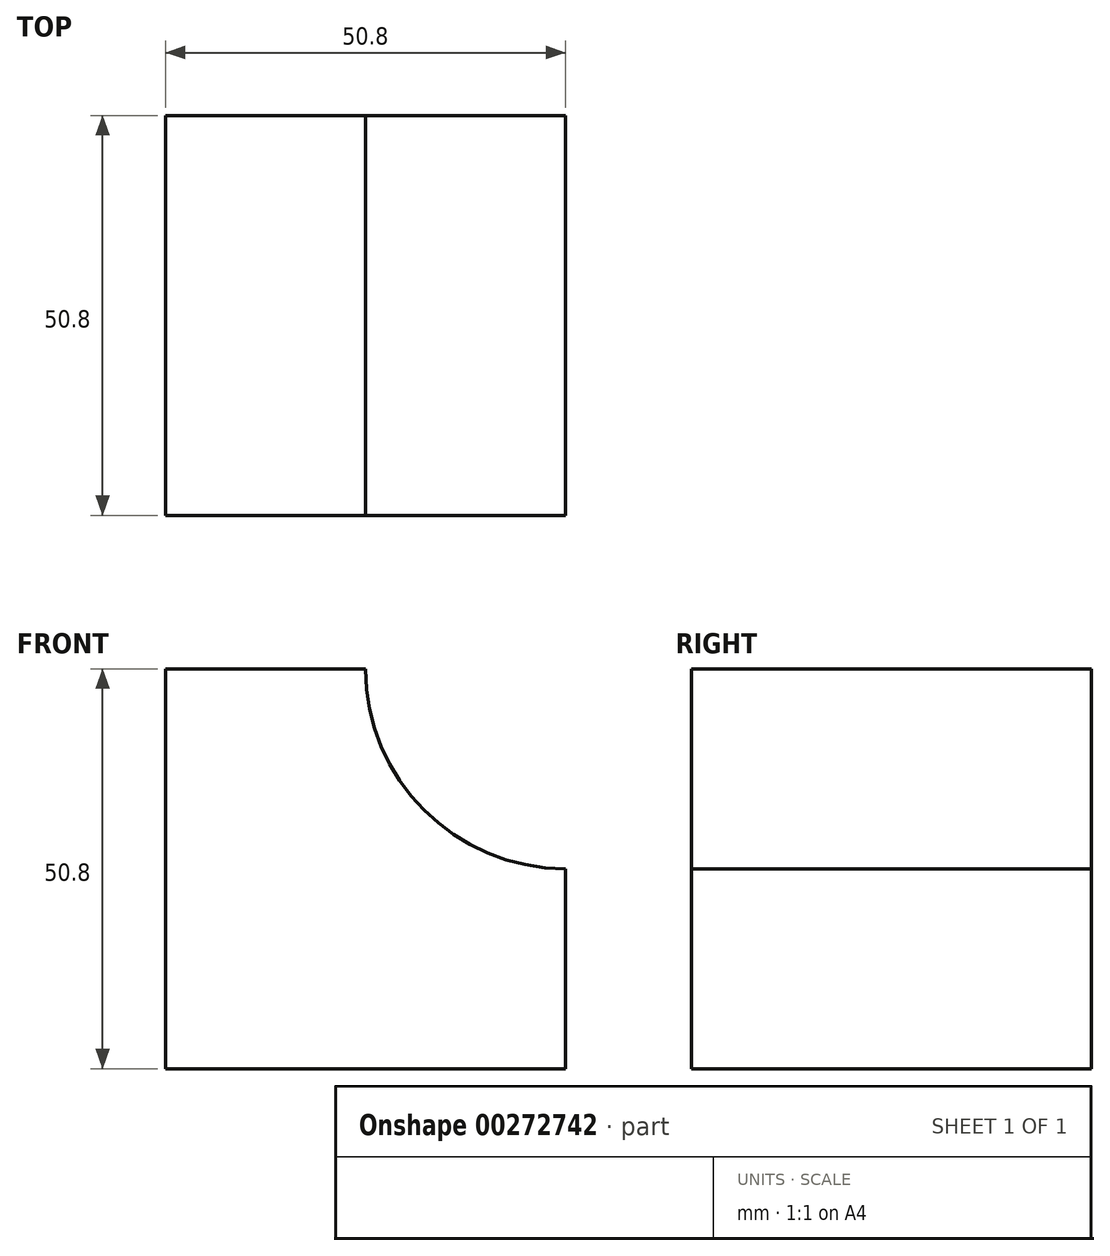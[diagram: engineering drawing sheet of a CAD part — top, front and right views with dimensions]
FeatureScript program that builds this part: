
annotation { "Feature Type Name" : "Feature", "Feature Type Description" : "" }
export const myFeature = defineFeature(function(context is Context, id is Id, definition is map)
    precondition{}
    {
        {
            var Q0;
            Q0=qCreatedBy(makeId("Front.planeOp"),FACE);
            var sketch = newSketch(context, id + "F0", { "sketchPlane" : qUnion([Q0])});
            skLineSegment(sketch, "E0", {"start": v(0, 0) * mm, "end": v(-50.8, 0) * mm});
            skLineSegment(sketch, "E1", {"start": v(-50.8, 0) * mm, "end": v(-50.8, 50.8) * mm});
            skLineSegment(sketch, "E2", {"start": v(-50.8, 50.8) * mm, "end": v(-25.4, 50.8) * mm});
            skLineSegment(sketch, "E3", {"start": v(-25.4, 50.8) * mm, "end": v(-25.4, 25.4) * mm});
            skLineSegment(sketch, "E4", {"start": v(-25.4, 25.4) * mm, "end": v(0, 25.4) * mm});
            skLineSegment(sketch, "E5", {"start": v(0, 0) * mm, "end": v(0, 25.4) * mm});
            skArc(sketch, "E6", {"start": v(-25.4, 50.8) * mm, "mid": v(-17.96, 32.84) * mm, "end": v(0, 25.4) * mm});
            skSolve(sketch);
        }
        {
            var Q0;
            Q0=makeQuery(id+"F0.imprint","IMPRINT",FACE,{"disambiguationData":[TD([[makeQuery(id+"F0.imprint","IMPRINT",EDGE,{"derivedFrom":sQuery(id+"F0.wireOp",EDGE,"E0")}),-1.0]])]});
            var Q1;
            Q1=makeQuery(id+"F0.imprint","IMPRINT",FACE,{"disambiguationData":[TD([[makeQuery(id+"F0.imprint","IMPRINT",EDGE,{"derivedFrom":sQuery(id+"F0.wireOp",EDGE,"E3")}),1.0]])]});
            extrude(context, id + "F1", {"entities" : qUnion([Q0, Q1]), "depth" : 50.8 * mm});
        }
    });
